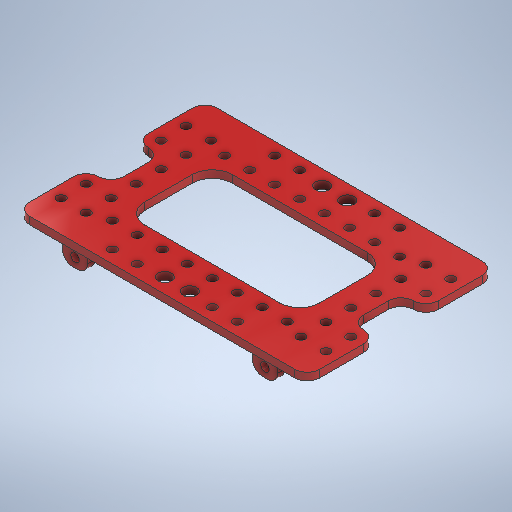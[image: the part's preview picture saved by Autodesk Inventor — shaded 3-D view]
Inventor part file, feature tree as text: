
AUTODESK INVENTOR PART (.ipt)
format: ipt  version: 2025 (Build 290162000, 162)  size: 1,016,832 bytes
history: native  units: mm
features: fillet x5, extrude x3, sketch x3
ambient origin geometry x8: Origin, YZ Plane, XZ Plane, XY Plane, X Axis, Y Axis, Z Axis, Center Point
bodies: Solide1 (feature_tree)
feature tree (11):
  extrude  "Extrusion1"  Depth=116.0mm
  fillet  "Congé1"  Radius=75.0mm
  fillet  "Congé2"  Radius=3.5mm
  extrude  "Extrusion2"  Depth=3.5mm
  extrude  "Extrusion3"  Depth=10.0mm
  fillet  "Congé3"  Radius=3.5mm
  fillet  "Congé4"  Radius=3.5mm
  fillet  "Congé5"  Radius=3.5mm
  sketch  "Esquisse1"
  sketch  "Esquisse2"
  sketch  "Esquisse3"
